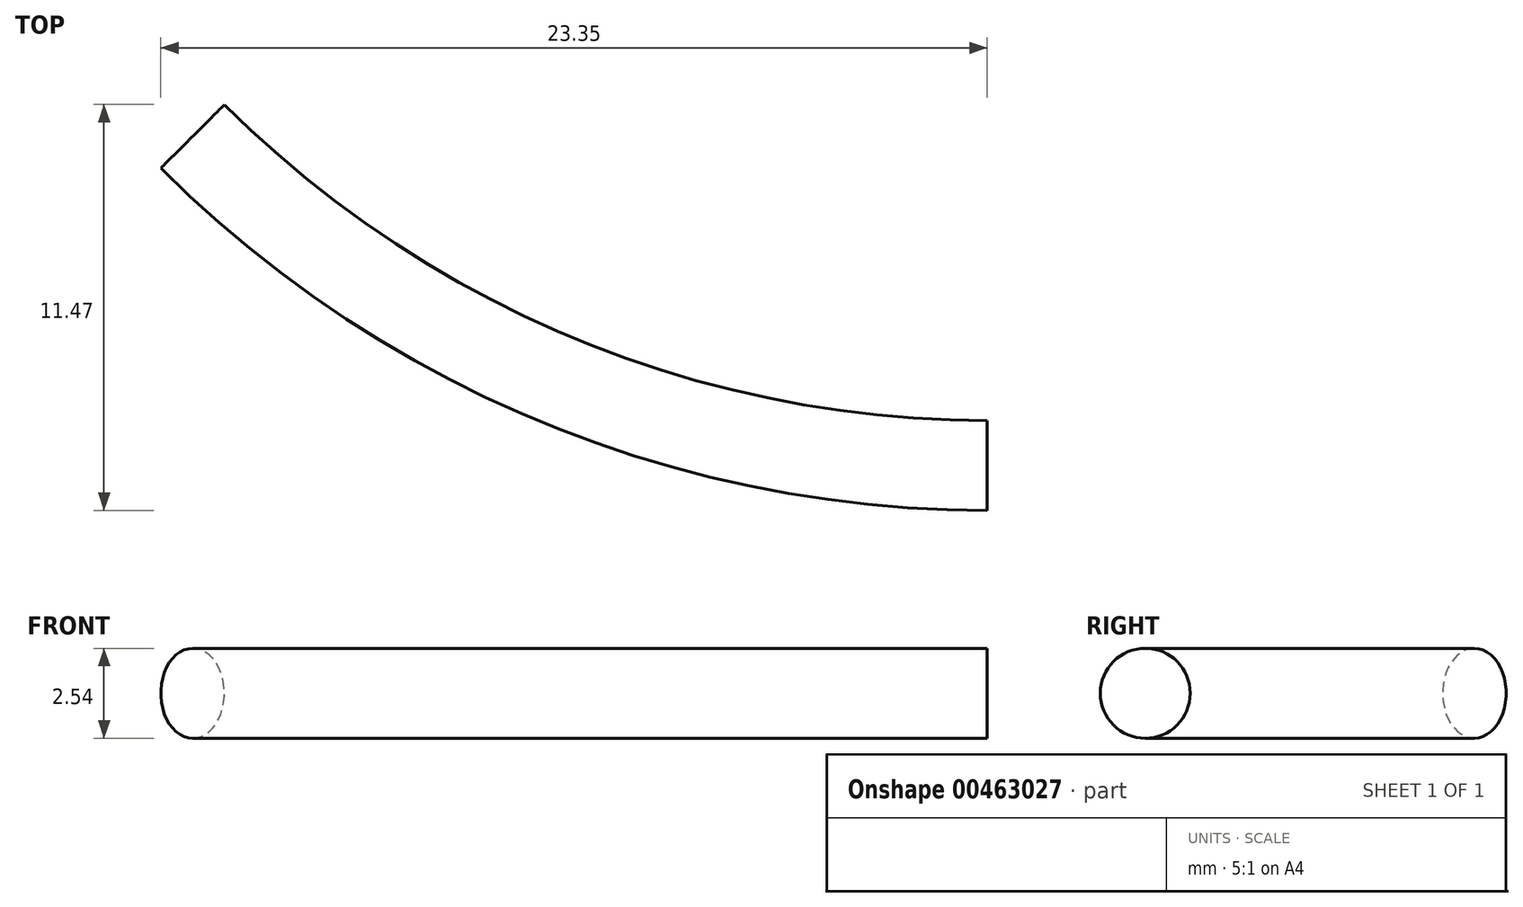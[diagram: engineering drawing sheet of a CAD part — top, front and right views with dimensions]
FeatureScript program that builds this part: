
annotation { "Feature Type Name" : "Feature", "Feature Type Description" : "" }
export const myFeature = defineFeature(function(context is Context, id is Id, definition is map)
    precondition{}
    {
        {
            var Q0;
            Q0=qCreatedBy(makeId("Top.planeOp"),FACE);
            var sketch = newSketch(context, id + "F0", { "sketchPlane" : qUnion([Q0])});
            skCircle(sketch, "E0", {"center": v(0, 0) * mm, "radius": 1.27 * mm});
            skSolve(sketch);
        }
        {
            var Q0;
            Q0=qCreatedBy(makeId("Right.planeOp"),FACE);
            var sketch = newSketch(context, id + "F1", { "sketchPlane" : qUnion([Q0])});
            skLineSegment(sketch, "E1", {"start": v(31.75, 17.7) * mm, "end": v(31.75, -29.03) * mm});
            skSolve(sketch);
        }
        {
            var Q0;
            Q0=qCreatedBy(makeId("Right.planeOp"),FACE);
            var sketch = newSketch(context, id + "F2", { "sketchPlane" : qUnion([Q0])});
            skCircle(sketch, "E2", {"center": v(0, 0) * mm, "radius": 1.27 * mm});
            skSolve(sketch);
        }
        {
            var Q0;
            Q0=makeQuery(id+"F2.imprint","IMPRINT",FACE,{"disambiguationData":[TD([[makeQuery(id+"F2.imprint","IMPRINT",EDGE,{"derivedFrom":sQuery(id+"F2.wireOp",EDGE,"E2")}),1.0]])]});
            var Q1;
            Q1=sQuery(id+"F1.wireOp",EDGE,"E1");
            revolve(context, id + "F3", {"entities" : qUnion([Q0]), "axis" : qUnion([Q1]), "revolveType" : RevolveType.ONE_DIRECTION, "angle" : 45 * degree});
        }
    });
